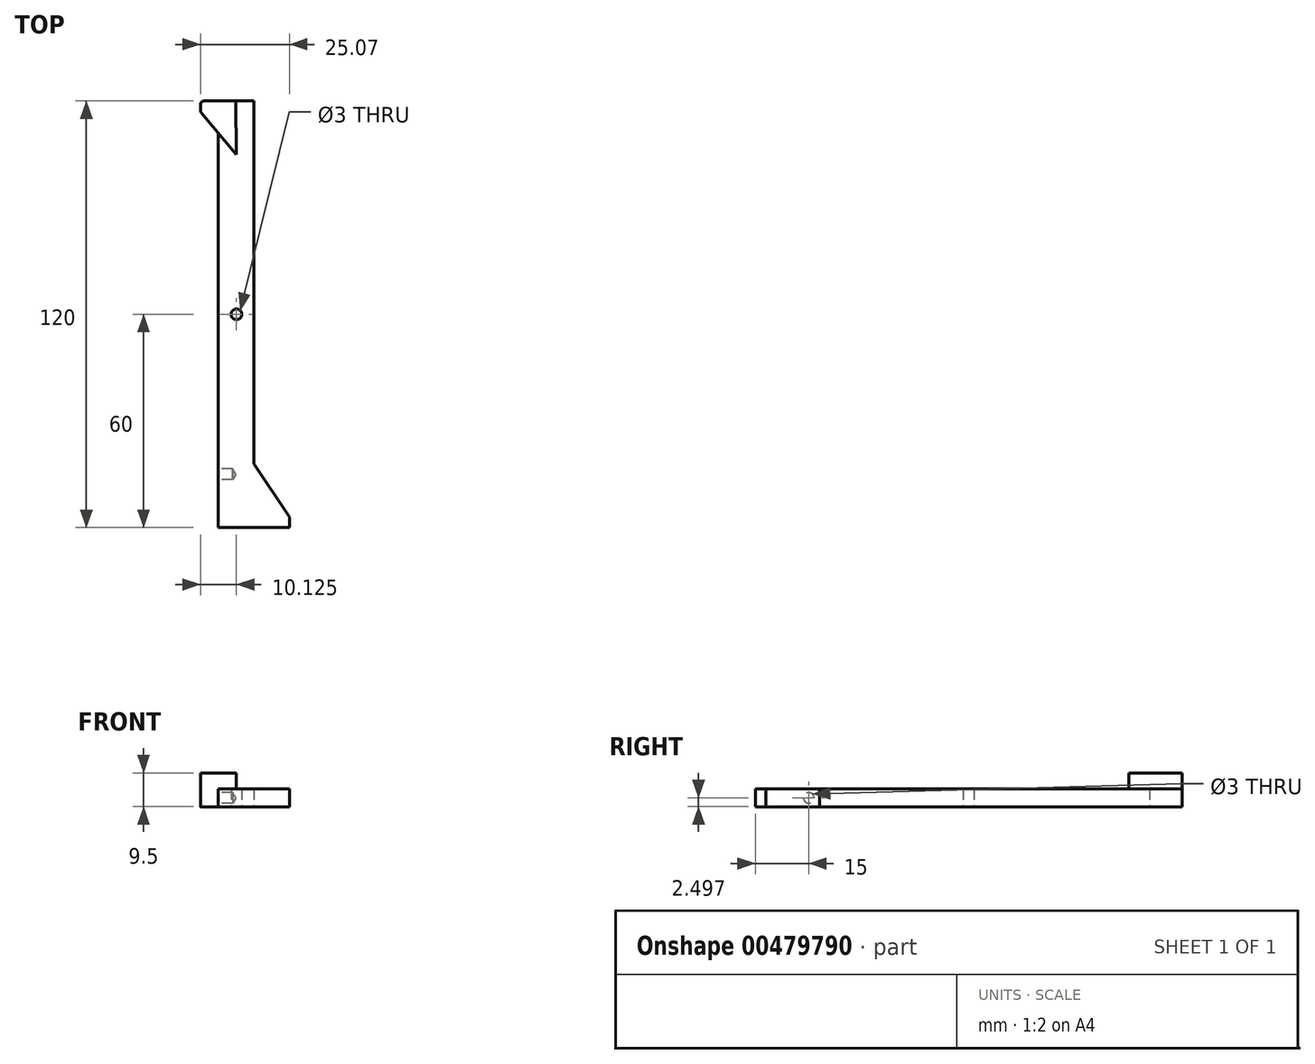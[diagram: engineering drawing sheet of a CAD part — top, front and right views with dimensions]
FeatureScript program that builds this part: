
annotation { "Feature Type Name" : "Feature", "Feature Type Description" : "" }
export const myFeature = defineFeature(function(context is Context, id is Id, definition is map)
    precondition{}
    {
        {
            var Q0;
            Q0=qCreatedBy(makeId("Right.planeOp"),FACE);
            var sketch = newSketch(context, id + "F0", { "sketchPlane" : qUnion([Q0])});
            skLineSegment(sketch, "E0.bottom", {"start": v(0, 5.07) * mm, "end": v(60, 5.07) * mm});
            skLineSegment(sketch, "E0.top", {"start": v(0, 15.07) * mm, "end": v(60, 15.07) * mm});
            skLineSegment(sketch, "E0.left", {"start": v(0, 5.07) * mm, "end": v(0, 15.07) * mm});
            skLineSegment(sketch, "E0.right", {"start": v(60, 5.07) * mm, "end": v(60, 15.07) * mm});
            skSolve(sketch);
        }
        {
            var Q0;
            Q0=makeQuery(id+"F0.imprint","IMPRINT",FACE,{"disambiguationData":[TD([[makeQuery(id+"F0.imprint","IMPRINT",EDGE,{"derivedFrom":sQuery(id+"F0.wireOp",EDGE,"E0.bottom")}),1.0]])]});
            extrude(context, id + "F1", {"entities" : qUnion([Q0]), "oppositeDirection" : true, "depth" : 5 * mm});
        }
        {
            var Q0;
            Q0=makeQuery(id+"F1.opExtrude","SWEPT_BODY",BODY,{"disambiguationData":[OSD([sQuery(id+"F0.wireOp",EDGE,"E0.bottom"),sQuery(id+"F0.wireOp",EDGE,"E0.top"),sQuery(id+"F0.wireOp",EDGE,"E0.left"),sQuery(id+"F0.wireOp",EDGE,"E0.right")])]});
            var Q1;
            Q1=qCreatedBy(makeId("Front.planeOp"),FACE);
            mirror(context, id + "F2", {"operationType" : NewBodyOperationType.ADD, "entities" : qUnion([Q0]), "mirrorPlane" : qUnion([Q1])});
        }
        {
            var Q0;
            Q0=qCreatedBy(makeId("Right.planeOp"),FACE);
            var sketch = newSketch(context, id + "F3", { "sketchPlane" : qUnion([Q0])});
            skLineSegment(sketch, "E1", {"start": v(-60, 15.07) * mm, "end": v(-60, 25.07) * mm});
            skLineSegment(sketch, "E2", {"start": v(-60, 25.07) * mm, "end": v(-57, 25.07) * mm});
            skLineSegment(sketch, "E3", {"start": v(-57, 25.07) * mm, "end": v(-42, 15.07) * mm});
            skLineSegment(sketch, "E4", {"start": v(-60, 15.07) * mm, "end": v(-42, 15.07) * mm});
            skSolve(sketch);
        }
        {
            var Q0;
            Q0=makeQuery(id+"F3.imprint","IMPRINT",FACE,{"disambiguationData":[TD([[makeQuery(id+"F3.imprint","IMPRINT",EDGE,{"derivedFrom":sQuery(id+"F3.wireOp",EDGE,"E1")}),-1.0]])]});
            extrude(context, id + "F4", {"entities" : qUnion([Q0]), "operationType" : NewBodyOperationType.ADD, "oppositeDirection" : true, "depth" : 5 * mm});
        }
        {
            var Q0;
            {var subQ0=makeQuery(id+"F1.opExtrude","CAP_FACE",FACE,{"disambiguationData":[OSD([sQuery(id+"F0.wireOp",EDGE,"E0.bottom"),sQuery(id+"F0.wireOp",EDGE,"E0.top"),sQuery(id+"F0.wireOp",EDGE,"E0.left"),sQuery(id+"F0.wireOp",EDGE,"E0.right")])],"isStart":true});Q0=makeQuery(id+"F4.boolean.opBoolean","MERGE",FACE,{"derivedFrom":[makeQuery(id+"F2.boolean.opBoolean","MERGE",FACE,{"derivedFrom":[subQ0,makeQuery(id+"F2.opPattern","COPY",FACE,{"derivedFrom":subQ0,"instanceName":"1"})]}),makeQuery(id+"F4.opExtrude","CAP_FACE",FACE,{"disambiguationData":[OSD([sQuery(id+"F3.wireOp",EDGE,"E1"),sQuery(id+"F3.wireOp",EDGE,"E2"),sQuery(id+"F3.wireOp",EDGE,"E3"),sQuery(id+"F3.wireOp",EDGE,"E4")])],"isStart":true})]});}
            var sketch = newSketch(context, id + "F5", { "sketchPlane" : qUnion([Q0])});
            skLineSegment(sketch, "E5", {"start": v(45, 10.03) * mm, "end": v(60, 10) * mm});
            skLineSegment(sketch, "E6", {"start": v(60, 0) * mm, "end": v(57, 0) * mm});
            skLineSegment(sketch, "E7", {"start": v(57, 0) * mm, "end": v(45, 10.03) * mm});
            skLineSegment(sketch, "E8", {"start": v(60, 10) * mm, "end": v(60, 0) * mm});
            skSolve(sketch);
        }
        {
            var Q0;
            Q0 = qSketchRegion(id + "F5", true);
            extrude(context, id + "F6", {"entities" : qUnion([Q0]), "operationType" : NewBodyOperationType.ADD, "oppositeDirection" : true, "depth" : 9.5 * mm});
        }
        {
            var Q0;
            {var subQ0=makeQuery(id+"F1.opExtrude","CAP_FACE",FACE,{"disambiguationData":[OSD([sQuery(id+"F0.wireOp",EDGE,"E0.bottom"),sQuery(id+"F0.wireOp",EDGE,"E0.top"),sQuery(id+"F0.wireOp",EDGE,"E0.left"),sQuery(id+"F0.wireOp",EDGE,"E0.right")])],"isStart":true});Q0=makeQuery(id+"F4.boolean.opBoolean","MERGE",FACE,{"derivedFrom":[makeQuery(id+"F2.boolean.opBoolean","MERGE",FACE,{"derivedFrom":[subQ0,makeQuery(id+"F2.opPattern","COPY",FACE,{"derivedFrom":subQ0,"instanceName":"1"})]}),makeQuery(id+"F4.opExtrude","CAP_FACE",FACE,{"disambiguationData":[OSD([sQuery(id+"F3.wireOp",EDGE,"E1"),sQuery(id+"F3.wireOp",EDGE,"E2"),sQuery(id+"F3.wireOp",EDGE,"E3"),sQuery(id+"F3.wireOp",EDGE,"E4")])],"isStart":true})]});}
            var sketch = newSketch(context, id + "F7", { "sketchPlane" : qUnion([Q0])});
            skCircle(sketch, "E9", {"center": v(0, 10.12) * mm, "radius": 1.5 * mm});
            skSolve(sketch);
        }
        {
            var Q0;
            Q0=sQuery(id+"F7.wireOp",VERTEX,"E9.center");
            var Q1;
            Q1=makeQuery(id+"F1.opExtrude","SWEPT_BODY",BODY,{"disambiguationData":[OSD([sQuery(id+"F0.wireOp",EDGE,"E0.bottom"),sQuery(id+"F0.wireOp",EDGE,"E0.top"),sQuery(id+"F0.wireOp",EDGE,"E0.left"),sQuery(id+"F0.wireOp",EDGE,"E0.right")])]});
            hole(context, id + "F8", {"style" : HoleStyle.SIMPLE, "endStyle" : HoleEndStyle.THROUGH, "holeDiameter" : 3 * mm, "isTappedThrough" : true, "tappedDepth" : 12 * mm, "tapClearance" : 3, "locations" : qUnion([Q0]), "scope" : qUnion([Q1])});
        }
        {
            var Q0;
            Q0=makeQuery(id+"F6.opExtrude","SWEPT_EDGE",EDGE,{"disambiguationData":[OSD([sQuery(id+"F5.wireOp",EDGE,"E6"),sQuery(id+"F5.wireOp",EDGE,"E7")])]});
            var Q1;
            Q1=makeQuery(id+"F6.opExtrude","SWEPT_EDGE",EDGE,{"disambiguationData":[OSD([sQuery(id+"F5.wireOp",EDGE,"E6"),sQuery(id+"F5.wireOp",EDGE,"E8")])]});
            fillet(context, id + "F9", {"entities" : qUnion([Q0, Q1]), "radius" : 1 * mm, "tangentPropagation" : true, "allowEdgeOverflow" : false});
        }
        {
            var Q0;
            {var subQ0=makeQuery(id+"F1.opExtrude","SWEPT_FACE",FACE,{"disambiguationData":[OSD([sQuery(id+"F0.wireOp",EDGE,"E0.bottom")])]});Q0=makeQuery(id+"F2.boolean.opBoolean","MERGE",FACE,{"derivedFrom":[subQ0,makeQuery(id+"F2.opPattern","COPY",FACE,{"derivedFrom":subQ0,"instanceName":"1"})]});}
            var sketch = newSketch(context, id + "F10", { "sketchPlane" : qUnion([Q0])});
            skCircle(sketch, "E10", {"center": v(-2.5, 45) * mm, "radius": 0.8 * mm});
            skSolve(sketch);
        }
        {
            var Q0;
            Q0=sQuery(id+"F10.wireOp",VERTEX,"E10.center");
            var Q1;
            Q1=makeQuery(id+"F1.opExtrude","SWEPT_BODY",BODY,{"disambiguationData":[OSD([sQuery(id+"F0.wireOp",EDGE,"E0.bottom"),sQuery(id+"F0.wireOp",EDGE,"E0.top"),sQuery(id+"F0.wireOp",EDGE,"E0.left"),sQuery(id+"F0.wireOp",EDGE,"E0.right")])]});
            hole(context, id + "F11", {"style" : HoleStyle.SIMPLE, "endStyle" : HoleEndStyle.BLIND, "holeDiameter" : 3 * mm, "holeDepth" : 4 * mm, "isTappedThrough" : true, "tappedDepth" : 12 * mm, "tapClearance" : 3, "locations" : qUnion([Q0]), "scope" : qUnion([Q1])});
        }
        {
            var Q0;
            Q0=makeQuery(id+"F1.opExtrude","SWEPT_BODY",BODY,{"disambiguationData":[OSD([sQuery(id+"F0.wireOp",EDGE,"E0.bottom"),sQuery(id+"F0.wireOp",EDGE,"E0.top"),sQuery(id+"F0.wireOp",EDGE,"E0.left"),sQuery(id+"F0.wireOp",EDGE,"E0.right")])]});
            var Q1;
            {var subQ0=makeQuery(id+"F1.opExtrude","CAP_EDGE",EDGE,{"disambiguationData":[OSD([sQuery(id+"F0.wireOp",EDGE,"E0.bottom")])],"isStart":false});Q1=makeQuery(id+"F2.boolean.opBoolean","MERGE",EDGE,{"derivedFrom":[subQ0,makeQuery(id+"F2.opPattern","COPY",EDGE,{"derivedFrom":subQ0,"instanceName":"1"})]});}
            transform(context, id + "F12", {"entities" : qUnion([Q0]), "transformType" : TransformType.ROTATION, "transformAxis" : qUnion([Q1]), "angle" : 90 * degree, "makeCopy" : false});
        }
    });
